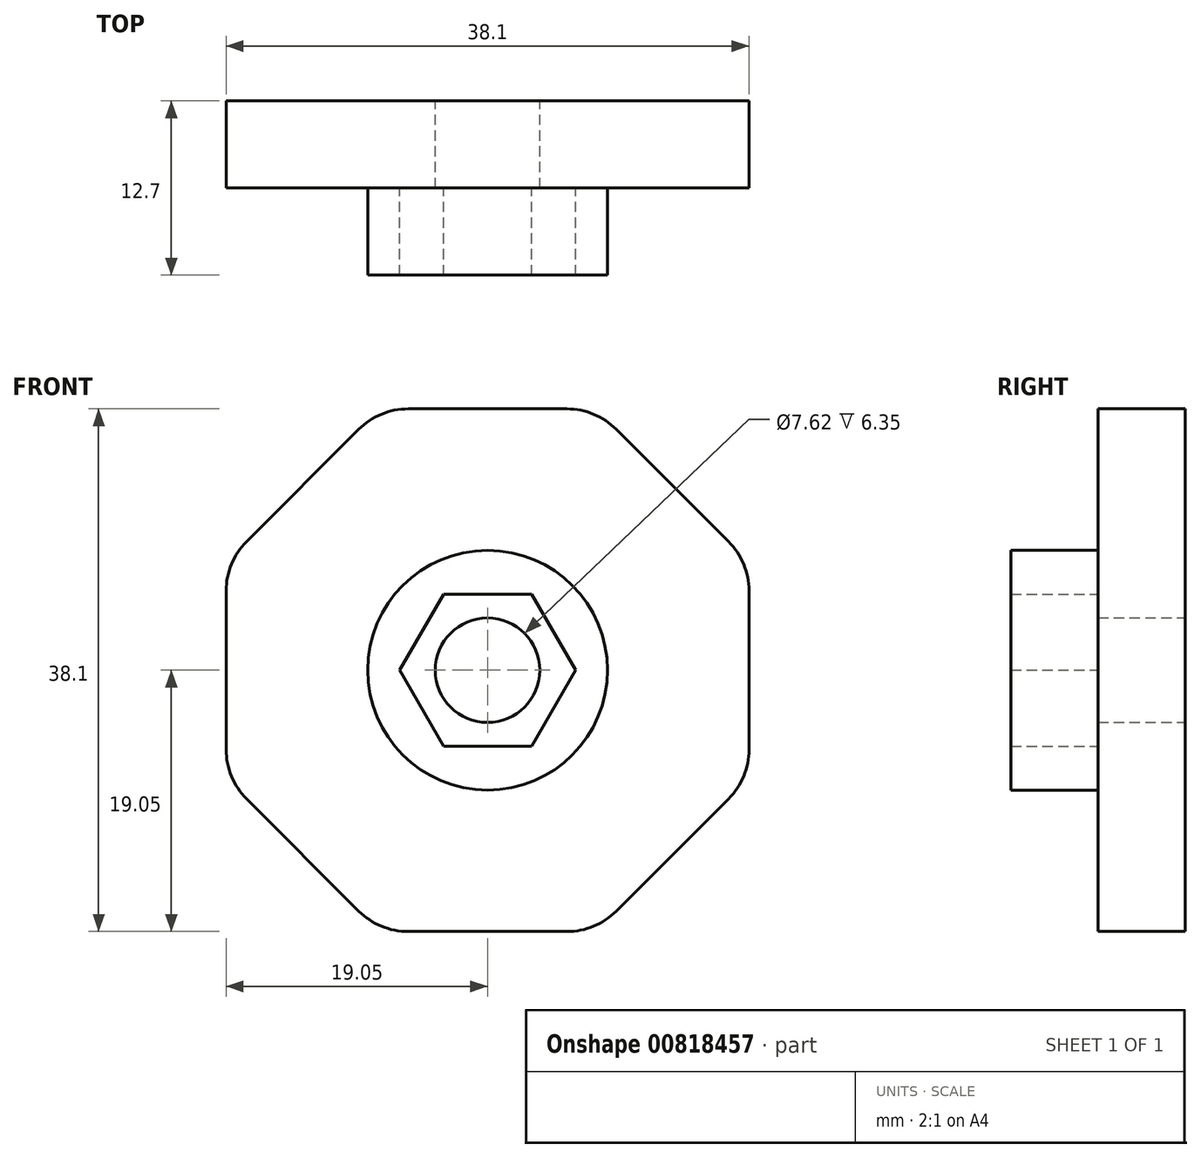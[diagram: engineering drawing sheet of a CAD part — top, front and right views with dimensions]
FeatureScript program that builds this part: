
annotation { "Feature Type Name" : "Feature", "Feature Type Description" : "" }
export const myFeature = defineFeature(function(context is Context, id is Id, definition is map)
    precondition{}
    {
        {
            var Q0;
            Q0=qCreatedBy(makeId("Front.planeOp"),FACE);
            var sketch = newSketch(context, id + "F0", { "sketchPlane" : qUnion([Q0])});
            skCircle(sketch, "E0.cCircle", {"center": v(0, 0) * mm, "radius": 19.05 * mm, "construction": true});
            skLineSegment(sketch, "E0.0", {"start": v(7.9, 19.05) * mm, "end": v(19.05, 7.9) * mm});
            skLineSegment(sketch, "E0.1", {"start": v(19.05, 7.9) * mm, "end": v(19.05, -7.9) * mm});
            skLineSegment(sketch, "E0.2", {"start": v(19.05, -7.9) * mm, "end": v(7.9, -19.05) * mm});
            skLineSegment(sketch, "E0.3", {"start": v(7.9, -19.05) * mm, "end": v(-7.9, -19.05) * mm});
            skLineSegment(sketch, "E0.4", {"start": v(-7.9, -19.05) * mm, "end": v(-19.05, -7.9) * mm});
            skLineSegment(sketch, "E0.5", {"start": v(-19.05, -7.9) * mm, "end": v(-19.05, 7.9) * mm});
            skLineSegment(sketch, "E0.6", {"start": v(-19.05, 7.9) * mm, "end": v(-7.9, 19.05) * mm});
            skLineSegment(sketch, "E0.7", {"start": v(-7.9, 19.05) * mm, "end": v(7.9, 19.05) * mm});
            skPoint(sketch, "E0.0.midPoint", {"position": v(13.47, 13.47) * mm});
            skCircle(sketch, "E1", {"center": v(0, 0) * mm, "radius": 3.81 * mm});
            skSolve(sketch);
        }
        {
            var Q0;
            Q0=makeQuery(id+"F0.imprint","IMPRINT",FACE,{"disambiguationData":[TD([[makeQuery(id+"F0.imprint","IMPRINT",EDGE,{"derivedFrom":sQuery(id+"F0.wireOp",EDGE,"E0.0")}),-1.0]])]});
            extrude(context, id + "F1", {"entities" : qUnion([Q0]), "depth" : 6.35 * mm, "offsetDistance" : 25.4 * mm});
        }
        {
            var Q0;
            Q0=makeQuery(id+"F1.opExtrude","CAP_FACE",FACE,{"disambiguationData":[OSD([sQuery(id+"F0.wireOp",EDGE,"E0.0"),sQuery(id+"F0.wireOp",EDGE,"E0.1"),sQuery(id+"F0.wireOp",EDGE,"E0.2"),sQuery(id+"F0.wireOp",EDGE,"E0.3"),sQuery(id+"F0.wireOp",EDGE,"E0.4"),sQuery(id+"F0.wireOp",EDGE,"E0.5"),sQuery(id+"F0.wireOp",EDGE,"E0.6"),sQuery(id+"F0.wireOp",EDGE,"E0.7"),sQuery(id+"F0.wireOp",EDGE,"E1")])],"isStart":false});
            var sketch = newSketch(context, id + "F2", { "sketchPlane" : qUnion([Q0])});
            skCircle(sketch, "E2", {"center": v(0, 0) * mm, "radius": 8.74 * mm});
            skCircle(sketch, "E3.cCircle", {"center": v(0, 0) * mm, "radius": 5.55 * mm, "construction": true});
            skLineSegment(sketch, "E3.0", {"start": v(-6.4, 0) * mm, "end": v(-3.2, 5.55) * mm});
            skLineSegment(sketch, "E3.1", {"start": v(-3.2, 5.55) * mm, "end": v(3.2, 5.55) * mm});
            skLineSegment(sketch, "E3.2", {"start": v(3.2, 5.55) * mm, "end": v(6.4, 0) * mm});
            skLineSegment(sketch, "E3.3", {"start": v(6.4, 0) * mm, "end": v(3.2, -5.55) * mm});
            skLineSegment(sketch, "E3.4", {"start": v(3.2, -5.55) * mm, "end": v(-3.2, -5.55) * mm});
            skLineSegment(sketch, "E3.5", {"start": v(-3.2, -5.55) * mm, "end": v(-6.4, 0) * mm});
            skPoint(sketch, "E3.0.midPoint", {"position": v(-4.8, 2.77) * mm});
            skSolve(sketch);
        }
        {
            var Q0;
            Q0=makeQuery(id+"F2.imprint","IMPRINT",FACE,{"disambiguationData":[TD([[makeQuery(id+"F2.imprint","IMPRINT",EDGE,{"derivedFrom":sQuery(id+"F2.wireOp",EDGE,"E2")}),1.0]])]});
            extrude(context, id + "F3", {"entities" : qUnion([Q0]), "operationType" : NewBodyOperationType.ADD, "depth" : 6.35 * mm, "offsetDistance" : 25.4 * mm});
        }
        {
            var Q0;
            Q0=makeQuery(id+"F1.opExtrude","SWEPT_EDGE",EDGE,{"disambiguationData":[OSD([sQuery(id+"F0.wireOp",EDGE,"E0.0"),sQuery(id+"F0.wireOp",EDGE,"E0.7")])]});
            var Q1;
            Q1=makeQuery(id+"F1.opExtrude","SWEPT_EDGE",EDGE,{"disambiguationData":[OSD([sQuery(id+"F0.wireOp",EDGE,"E0.0"),sQuery(id+"F0.wireOp",EDGE,"E0.1")])]});
            var Q2;
            Q2=makeQuery(id+"F1.opExtrude","SWEPT_EDGE",EDGE,{"disambiguationData":[OSD([sQuery(id+"F0.wireOp",EDGE,"E0.1"),sQuery(id+"F0.wireOp",EDGE,"E0.2")])]});
            var Q3;
            Q3=makeQuery(id+"F1.opExtrude","SWEPT_EDGE",EDGE,{"disambiguationData":[OSD([sQuery(id+"F0.wireOp",EDGE,"E0.2"),sQuery(id+"F0.wireOp",EDGE,"E0.3")])]});
            var Q4;
            Q4=makeQuery(id+"F1.opExtrude","SWEPT_EDGE",EDGE,{"disambiguationData":[OSD([sQuery(id+"F0.wireOp",EDGE,"E0.3"),sQuery(id+"F0.wireOp",EDGE,"E0.4")])]});
            var Q5;
            Q5=makeQuery(id+"F1.opExtrude","SWEPT_EDGE",EDGE,{"disambiguationData":[OSD([sQuery(id+"F0.wireOp",EDGE,"E0.4"),sQuery(id+"F0.wireOp",EDGE,"E0.5")])]});
            var Q6;
            Q6=makeQuery(id+"F1.opExtrude","SWEPT_EDGE",EDGE,{"disambiguationData":[OSD([sQuery(id+"F0.wireOp",EDGE,"E0.5"),sQuery(id+"F0.wireOp",EDGE,"E0.6")])]});
            var Q7;
            Q7=makeQuery(id+"F1.opExtrude","SWEPT_EDGE",EDGE,{"disambiguationData":[OSD([sQuery(id+"F0.wireOp",EDGE,"E0.6"),sQuery(id+"F0.wireOp",EDGE,"E0.7")])]});
            fillet(context, id + "F4", {"entities" : qUnion([Q0, Q1, Q2, Q3, Q4, Q5, Q6, Q7]), "radius" : 5.08 * mm, "tangentPropagation" : true, "allowEdgeOverflow" : false});
        }
    });
